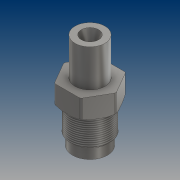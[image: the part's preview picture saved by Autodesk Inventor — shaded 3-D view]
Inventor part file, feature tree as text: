
AUTODESK INVENTOR PART (.ipt)
format: ipt  version: 2021 (Build 250183000, 183)  size: 219,648 bytes
history: native  units: mm
features: sketch x12, extrude x7, revolve x2, fillet x2, projected_geometry x2, plane x1, mirror x1, chamfer x1, thread x1, sweep x1
ambient origin geometry x8: Origin, YZ Plane, XZ Plane, XY Plane, X Axis, Y Axis, Z Axis, Center Point
bodies: Solid1 (feature_tree)
feature tree (30):
  extrude  "Extrusion1"  TaperAngle=90.0deg  [1 undecoded]
  revolve  "Revolution1"  [1 undecoded]
  plane  "Work Plane1"
  sketch  "Sketch3"  dims[d8=12.0mm d9=15.0mm d10=0.0mm]
  mirror  "Mirror1"
  extrude  "Extrusion2"  Depth=15.0mm TaperAngle=0.0deg
  extrude  "Extrusion3"  Depth=4.0mm TaperAngle=0.0deg
  extrude  "Extrusion4"  Depth=2.5mm TaperAngle=0.0deg
  chamfer  "Chamfer1"  Distance=4.0mm Angle=45.0deg
  extrude  "Extrusion5"  Depth=10.5mm TaperAngle=0.0deg
  extrude  "Extrusion6"  Depth=1.0mm TaperAngle=0.0deg
  fillet  "Fillet1"  Radius=1.0mm
  thread  "Thread1"  [1 undecoded]
  extrude  "Extrusion7"  Depth=15.0mm TaperAngle=0.0deg
  revolve  "Revolution2"  Angle=90.0deg
  sweep  "Sweep1"
  fillet  "Fillet2"  Radius=1.0mm
  sketch  "Sketch1"  dims[d2=8.0mm d3=0.0mm d4=90.0deg]
  sketch  "Sketch2"  dims[d5=-5.75mm d7=21.0mm]
  projected_geometry  "Projected Loop1"
  projected_geometry  "Projected Loop2"
  sketch  "Sketch4"  dims[d11=7.0mm d12=4.0mm d13=0.0mm]
  sketch  "Sketch5"  dims[d14=3.5mm d15=2.5mm d16=0.0mm d17=4.0mm d18=1.75mm d19=45.0deg]
  sketch  "Sketch6"  dims[d20=16.0mm d21=10.5mm d22=0.0mm]
  sketch  "Sketch7"  dims[d23=14.0mm d24=5.0mm d25=0.0mm d26=1.0mm d27=15.5mm d28=0.5mm]
  sketch  "Sketch8"  dims[d29=8.0mm d30=15.0mm d31=0.0mm]
  sketch  "Sketch9"  dims[d32=0.75mm d33=90.0deg]
  sketch  "Sketch10"  dims[d34=1.5mm d38=0.0mm d39=0.0mm d40=1.0mm]
  sketch  "Sketch11"
  sketch  "Sketch12"
note: 3 required parameter values undecoded (feature->parameter linkage not recoverable at this tier; creation-order binding heuristic only, values carry confidence <= 0.55)